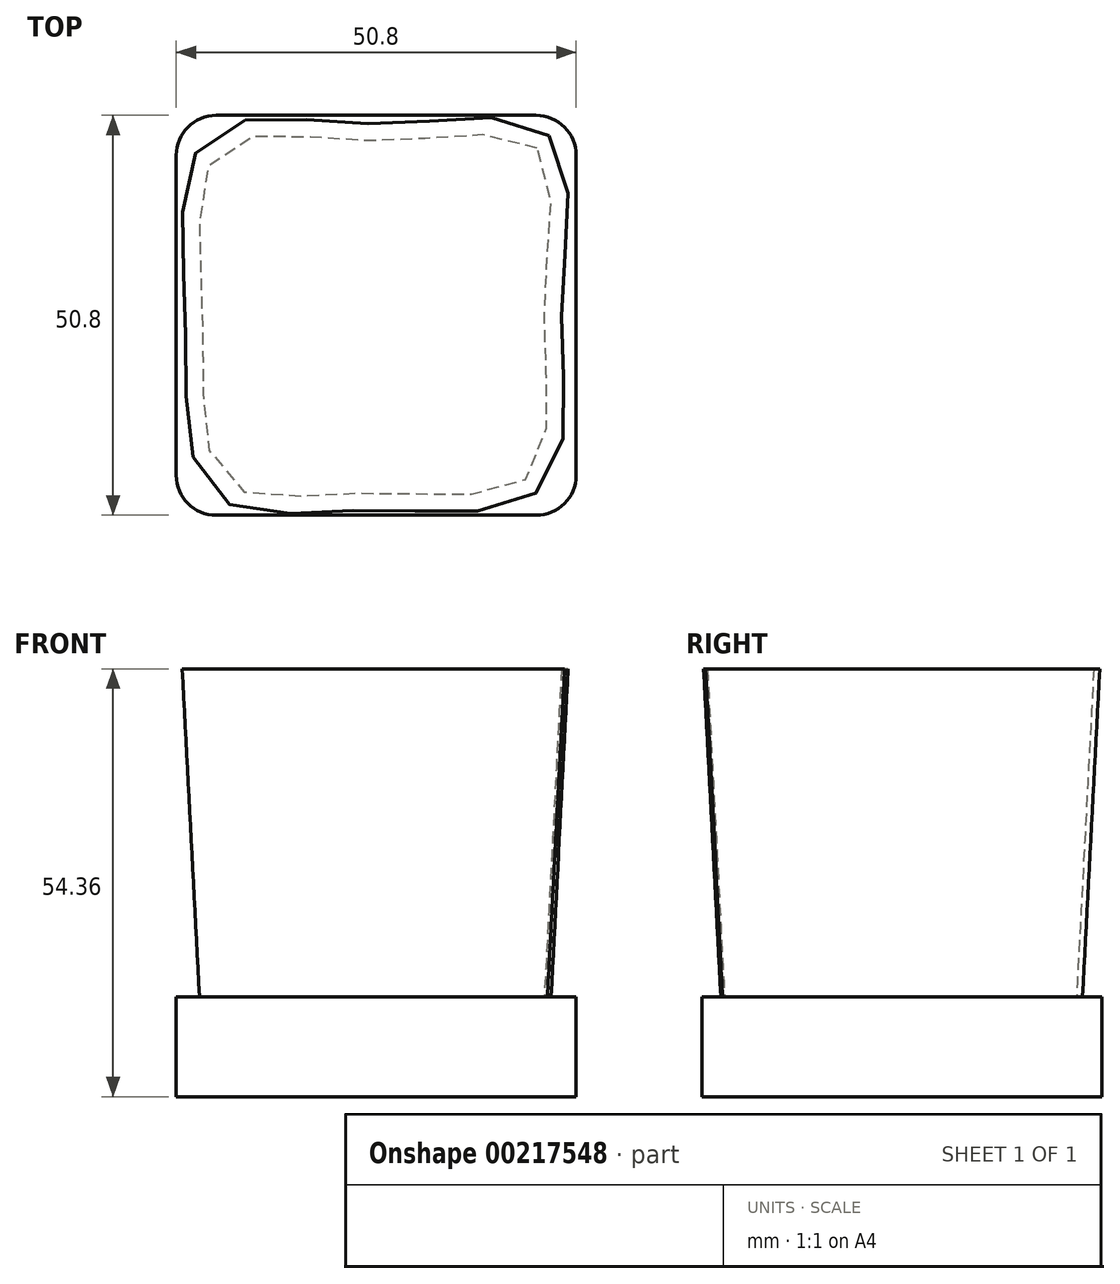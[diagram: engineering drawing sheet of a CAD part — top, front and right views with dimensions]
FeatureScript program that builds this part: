
annotation { "Feature Type Name" : "Feature", "Feature Type Description" : "" }
export const myFeature = defineFeature(function(context is Context, id is Id, definition is map)
    precondition{}
    {
        {
            var Q0;
            Q0=qCreatedBy(makeId("Top.planeOp"),FACE);
            var sketch = newSketch(context, id + "F0", { "sketchPlane" : qUnion([Q0])});
            skLineSegment(sketch, "E0.bottom", {"start": v(0, 0) * mm, "end": v(-50.8, 0) * mm});
            skLineSegment(sketch, "E0.top", {"start": v(0, 50.8) * mm, "end": v(-50.8, 50.8) * mm});
            skLineSegment(sketch, "E0.left", {"start": v(0, 0) * mm, "end": v(0, 50.8) * mm});
            skLineSegment(sketch, "E0.right", {"start": v(-50.8, 0) * mm, "end": v(-50.8, 50.8) * mm});
            skSolve(sketch);
        }
        {
            var Q0;
            Q0 = qSketchRegion(id + "F0", true);
            extrude(context, id + "F1", {"entities" : qUnion([Q0]), "oppositeDirection" : true, "depth" : 12.7 * mm});
        }
        {
            var Q0;
            Q0=makeQuery(id+"F1.opExtrude","SWEPT_EDGE",EDGE,{"disambiguationData":[OSD([sQuery(id+"F0.wireOp",EDGE,"E0.top"),sQuery(id+"F0.wireOp",EDGE,"E0.left")])]});
            var Q1;
            Q1=makeQuery(id+"F1.opExtrude","SWEPT_EDGE",EDGE,{"disambiguationData":[OSD([sQuery(id+"F0.wireOp",EDGE,"E0.bottom"),sQuery(id+"F0.wireOp",EDGE,"E0.left")])]});
            var Q2;
            Q2=makeQuery(id+"F1.opExtrude","SWEPT_EDGE",EDGE,{"disambiguationData":[OSD([sQuery(id+"F0.wireOp",EDGE,"E0.bottom"),sQuery(id+"F0.wireOp",EDGE,"E0.right")])]});
            var Q3;
            Q3=makeQuery(id+"F1.opExtrude","SWEPT_EDGE",EDGE,{"disambiguationData":[OSD([sQuery(id+"F0.wireOp",EDGE,"E0.top"),sQuery(id+"F0.wireOp",EDGE,"E0.right")])]});
            fillet(context, id + "F2", {"entities" : qUnion([Q0, Q1, Q2, Q3]), "radius" : 5.08 * mm, "tangentPropagation" : true, "allowEdgeOverflow" : false});
        }
        {
            var Q0;
            Q0=qCreatedBy(makeId("Top.planeOp"),FACE);
            var sketch = newSketch(context, id + "F3", { "sketchPlane" : qUnion([Q0])});
            skLineSegment(sketch, "E1.bottom", {"start": v(-43.18, 43.18) * mm, "end": v(-7.62, 43.18) * mm});
            skLineSegment(sketch, "E1.top", {"start": v(-43.18, 7.62) * mm, "end": v(-7.62, 7.62) * mm});
            skLineSegment(sketch, "E1.left", {"start": v(-43.18, 43.18) * mm, "end": v(-43.18, 7.62) * mm});
            skLineSegment(sketch, "E1.right", {"start": v(-7.62, 43.18) * mm, "end": v(-7.62, 7.62) * mm});
            skSolve(sketch);
        }
        {
            var Q0;
            Q0 = qSketchRegion(id + "F3", true);
            extrude(context, id + "F4", {"entities" : qUnion([Q0]), "operationType" : NewBodyOperationType.ADD, "depth" : 38.1 * mm});
        }
        {
            var Q0;
            Q0=qCreatedBy(makeId("Top.planeOp"),FACE);
            var sketch = newSketch(context, id + "F5", { "sketchPlane" : qUnion([Q0])});
            skFitSpline(sketch, "E2", {"points": [v(-44.54, 4.3) * mm, v(-47.47, 25.02) * mm, v(-45.27, 46.47) * mm, v(-25.11, 47.57) * mm, v(-4.95, 46.65) * mm, v(-4.03, 26.49) * mm, v(-5.87, 5.04) * mm, v(-26.58, 2.84) * mm, v(-44.54, 4.3) * mm]});
            skSolve(sketch);
        }
        {
            var Q0;
            Q0 = qSketchRegion(id + "F5", true);
            extrude(context, id + "F6", {"entities" : qUnion([Q0]), "operationType" : NewBodyOperationType.ADD, "depth" : 41.66 * mm, "hasDraft" : true, "draftAngle" : 3 * degree});
        }
    });
